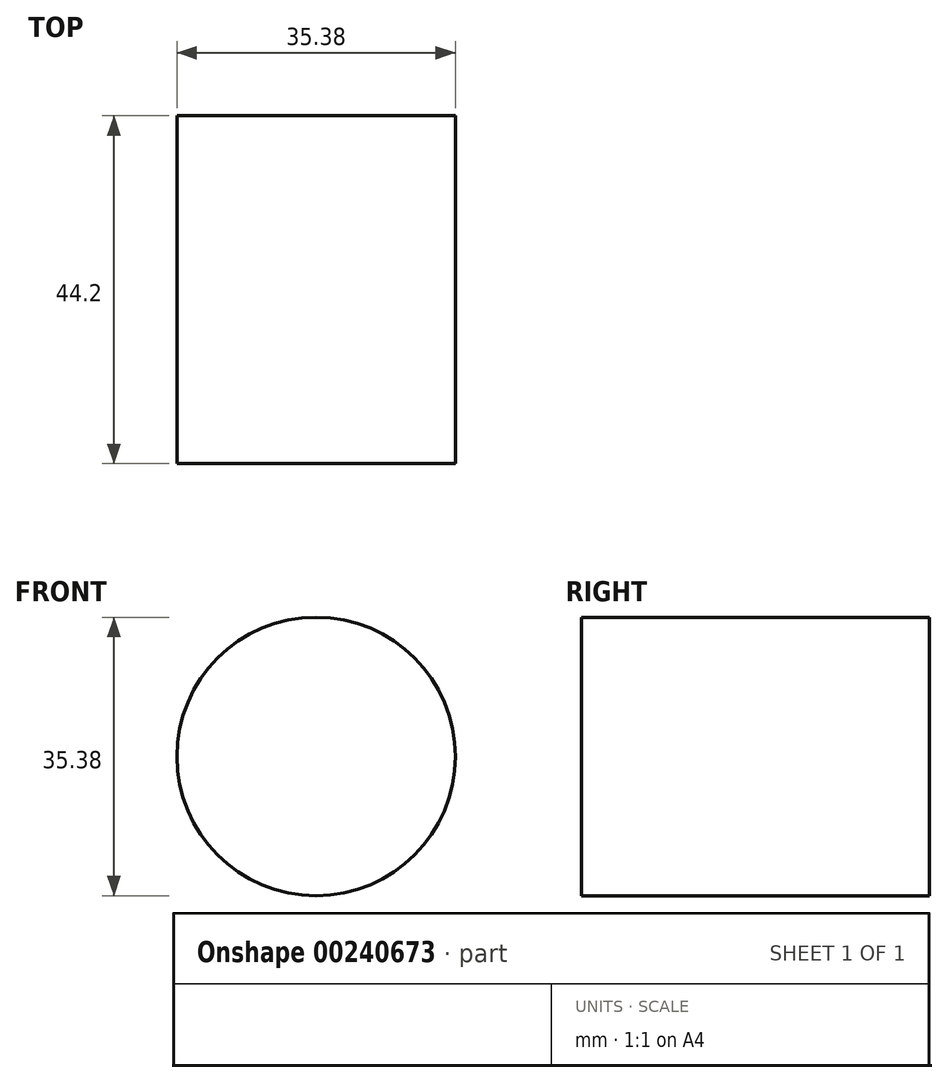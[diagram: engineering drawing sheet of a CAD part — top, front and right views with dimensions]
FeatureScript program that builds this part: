
annotation { "Feature Type Name" : "Feature", "Feature Type Description" : "" }
export const myFeature = defineFeature(function(context is Context, id is Id, definition is map)
    precondition{}
    {
        {
            var Q0;
            Q0=qCreatedBy(makeId("Front.planeOp"),FACE);
            var sketch = newSketch(context, id + "F0", { "sketchPlane" : qUnion([Q0])});
            skCircle(sketch, "E0", {"center": v(0, 0) * mm, "radius": 17.69 * mm});
            skSolve(sketch);
        }
        {
            var Q0;
            Q0=makeQuery(id+"F0.imprint","IMPRINT",FACE,{"disambiguationData":[TD([[makeQuery(id+"F0.imprint","IMPRINT",EDGE,{"derivedFrom":sQuery(id+"F0.wireOp",EDGE,"E0")}),1.0]])]});
            extrude(context, id + "F1", {"entities" : qUnion([Q0]), "depth" : 44.2 * mm});
        }
    });
